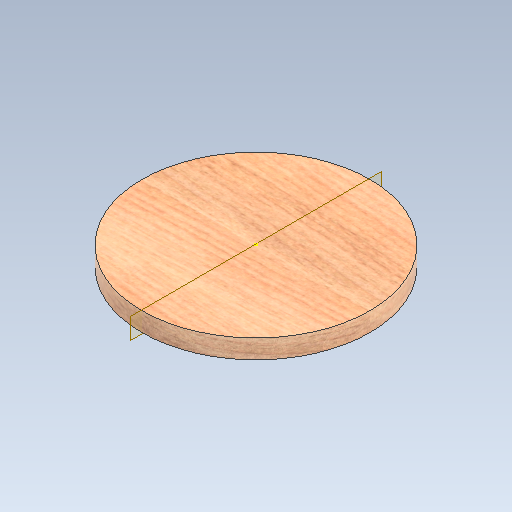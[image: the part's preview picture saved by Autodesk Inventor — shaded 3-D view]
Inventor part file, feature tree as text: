
AUTODESK INVENTOR PART (.ipt)
format: ipt  version: 2021 (Build 250183000, 183)  size: 189,440 bytes
history: native  units: in
note: dims shown in document units (in); Inventor stores cm internally (conversion verified against a paired STEP export)
features: sketch x2, extrude x1
ambient origin geometry x8: Origin, YZ Plane, XZ Plane, XY Plane, X Axis, Y Axis, Z Axis, Center Point
bodies: Solid1 (feature_tree)
feature tree (3):
  extrude  "Extrusion1"  Depth=1.0in TaperAngle=0.0deg
  sketch  "Sketch2"
  sketch  "Sketch1"  dims[d0=12.0in d1=1.0in d2=0.0in]
